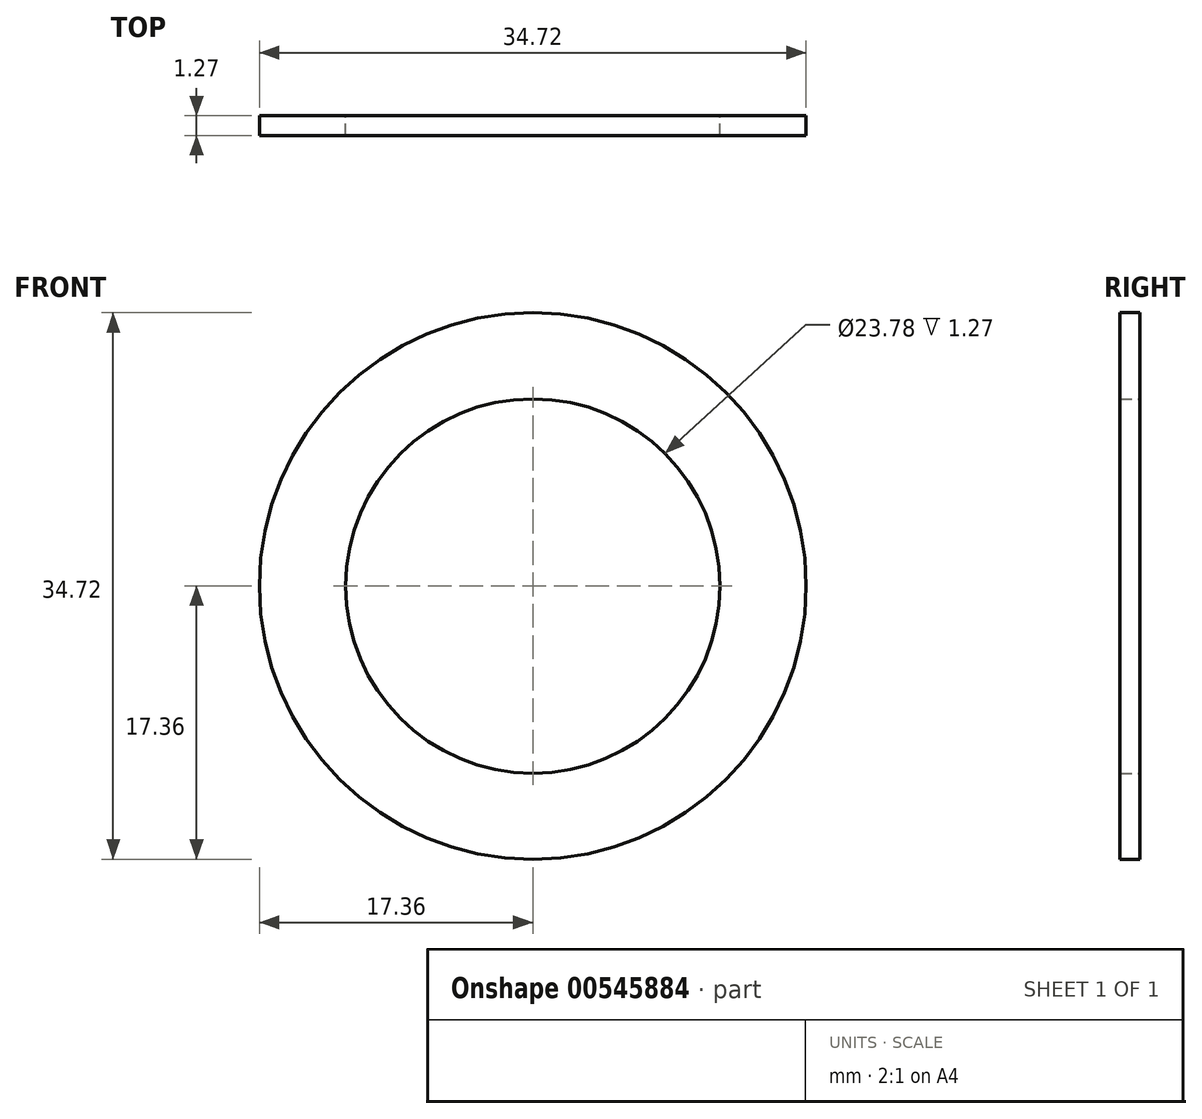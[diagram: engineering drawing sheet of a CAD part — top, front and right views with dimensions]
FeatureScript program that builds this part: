
annotation { "Feature Type Name" : "Feature", "Feature Type Description" : "" }
export const myFeature = defineFeature(function(context is Context, id is Id, definition is map)
    precondition{}
    {
        {
            var Q0;
            Q0=qCreatedBy(makeId("Front.planeOp"),FACE);
            var sketch = newSketch(context, id + "F0", { "sketchPlane" : qUnion([Q0])});
            skCircle(sketch, "E0", {"center": v(0, 0) * mm, "radius": 17.36 * mm});
            skCircle(sketch, "E1", {"center": v(0, 0) * mm, "radius": 11.89 * mm});
            skSolve(sketch);
        }
        {
            var Q0;
            Q0 = qSketchRegion(id + "F0", true);
            extrude(context, id + "F1", {"entities" : qUnion([Q0]), "depth" : 1.27 * mm, "offsetDistance" : 25.4 * mm});
        }
    });
